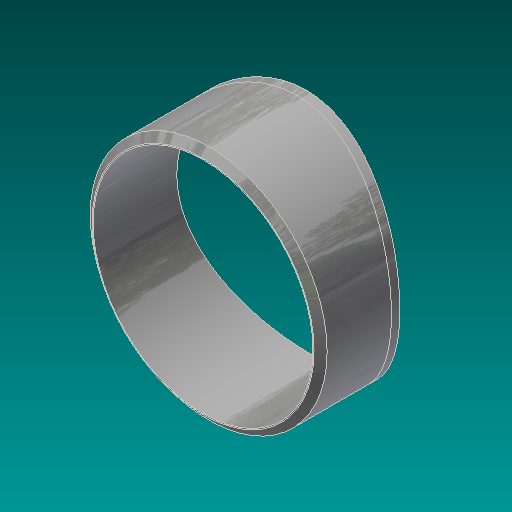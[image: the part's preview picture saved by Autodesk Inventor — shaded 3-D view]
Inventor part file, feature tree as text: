
AUTODESK INVENTOR PART (.ipt)
format: ipt  version: 2017.3 (Build 213257000, 257)  size: 237,568 bytes
history: native  units: in
note: dims shown in document units (in); Inventor stores cm internally (conversion verified against a paired STEP export)
features: extrude x5, other x5, sketch x3, split x3, chamfer x1, loft x1
ambient origin geometry x8: Origin, YZ Plane, XZ Plane, XY Plane, X Axis, Y Axis, Z Axis, Center Point
bodies: Solid1 (feature_tree)
feature tree (18):
  extrude  "Extrusion1"  Depth=13.0in
  sketch  "Sketch2"  dims[d2=22.0106in d3=0.0in d4=34.125in d5=20.1562in d6=0.0in]
  extrude  "Extrusion2"  Depth=34.125in
  split  "Split1"
  split  "Split2"
  chamfer  "Chamfer1"  Distance=20.1562in
  split  "Split3"
  loft  "Loft1"
  sketch  "Sketch1"  dims[d0=14.0in d1=13.0in]
  other  "Srf1"
  other  "Srf2"
  sketch  "Sketch3"  dims[d7=34.75in d8=35.75in d9=0.0in d10=0.0in d11=0.0in d12=0.0in d13=0.4375in d14=0.125in d15=0.2577in d16=13.125in d17=1.0in d18=0.0in d19=0.0in d20=90.0deg d21=0.0in d22=90.0deg]
  other  "Srf3"
  other  "Edges1"
  other  "Edges2"
  extrude  "ExtrusionSrf1"  TaperAngle=0.0deg  [1 undecoded]
  extrude  "ExtrusionSrf2"  TaperAngle=0.0deg  [1 undecoded]
  extrude  "ExtrusionSrf3"  Depth=0.4375in
note: 2 required parameter values undecoded (feature->parameter linkage not recoverable at this tier; creation-order binding heuristic only, values carry confidence <= 0.55)
